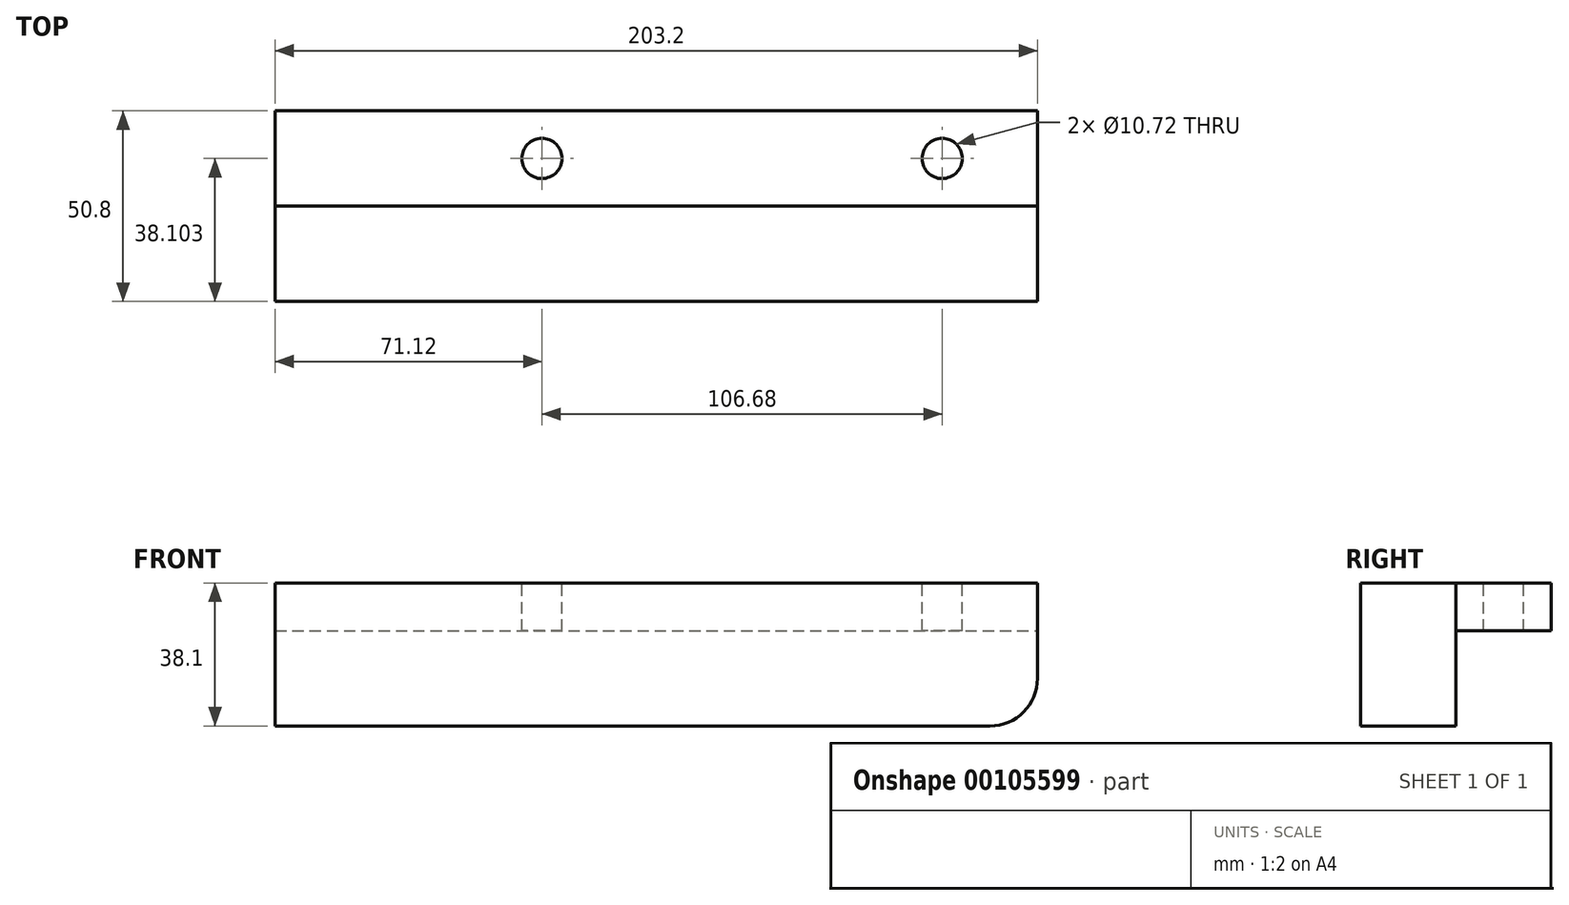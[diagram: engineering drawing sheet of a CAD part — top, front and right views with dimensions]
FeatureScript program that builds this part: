
annotation { "Feature Type Name" : "Feature", "Feature Type Description" : "" }
export const myFeature = defineFeature(function(context is Context, id is Id, definition is map)
    precondition{}
    {
        {
            var Q0;
            Q0=qCreatedBy(makeId("Top.planeOp"),FACE);
            var sketch = newSketch(context, id + "F0", { "sketchPlane" : qUnion([Q0])});
            skLineSegment(sketch, "E0.bottom", {"start": v(-101.6, 22.18) * mm, "end": v(101.6, 22.18) * mm});
            skLineSegment(sketch, "E0.top", {"start": v(-101.6, -28.62) * mm, "end": v(88.9, -28.62) * mm});
            skLineSegment(sketch, "E0.left", {"start": v(-101.6, 22.18) * mm, "end": v(-101.6, -28.62) * mm});
            skLineSegment(sketch, "E0.right", {"start": v(101.6, 22.18) * mm, "end": v(101.6, -15.92) * mm});
            skPoint(sketch, "E0.middle", {"position": v(0, -3.22) * mm});
            skLineSegment(sketch, "E1", {"start": v(-101.6, -3.22) * mm, "end": v(101.6, -3.22) * mm});
            skPoint(sketch, "E2.visualSharp", {"position": v(101.6, -28.62) * mm});
            skLineSegment(sketch, "E3", {"start": v(88.9, -28.62) * mm, "end": v(101.6, -28.62) * mm});
            skLineSegment(sketch, "E4", {"start": v(101.6, -15.92) * mm, "end": v(101.6, -28.62) * mm});
            skSolve(sketch);
        }
        {
            var Q0;
            {var subQ0=sQuery(id+"F0.wireOp",EDGE,"E0.bottom");Q0=makeQuery(id+"F0.imprint","IMPRINT",FACE,{"disambiguationData":[TD([[makeQuery(id+"F0.imprint","IMPRINT",EDGE,{"derivedFrom":subQ0}),-1.0]])]});}
            extrude(context, id + "F1", {"entities" : qUnion([Q0]), "oppositeDirection" : true, "depth" : 12.7 * mm});
        }
        {
            var Q0;
            {var subQ0=sQuery(id+"F0.wireOp",EDGE,"E0.top");Q0=makeQuery(id+"F0.imprint","IMPRINT",FACE,{"disambiguationData":[TD([[makeQuery(id+"F0.imprint","IMPRINT",EDGE,{"derivedFrom":subQ0}),1.0]])]});}
            extrude(context, id + "F2", {"entities" : qUnion([Q0]), "oppositeDirection" : true, "depth" : 38.1 * mm});
        }
        {
            var Q0;
            Q0=makeQuery(id+"F1.opExtrude","CAP_FACE",FACE,{"disambiguationData":[OSD([sQuery(id+"F0.wireOp",EDGE,"E0.bottom"),sQuery(id+"F0.wireOp",EDGE,"E0.left"),sQuery(id+"F0.wireOp",EDGE,"E0.right"),sQuery(id+"F0.wireOp",EDGE,"E1")])],"isStart":true});
            var sketch = newSketch(context, id + "F3", { "sketchPlane" : qUnion([Q0])});
            skPoint(sketch, "E5", {"position": v(76.2, 9.48) * mm});
            skPoint(sketch, "E6", {"position": v(-30.48, 9.48) * mm});
            skSolve(sketch);
        }
        {
            var Q0;
            Q0=sQuery(id+"F3.wireOp",VERTEX,"E6");
            var Q1;
            Q1=sQuery(id+"F3.wireOp",VERTEX,"E5");
            var Q2;
            Q2=makeQuery(id+"F1.opExtrude","SWEPT_BODY",BODY,{"disambiguationData":[OSD([sQuery(id+"F0.wireOp",EDGE,"E0.bottom"),sQuery(id+"F0.wireOp",EDGE,"E0.left"),sQuery(id+"F0.wireOp",EDGE,"E0.right"),sQuery(id+"F0.wireOp",EDGE,"E1")])]});
            hole(context, id + "F4", {"style" : HoleStyle.SIMPLE, "endStyle" : HoleEndStyle.BLIND, "holeDiameter" : 10.72 * mm, "holeDepth" : 50.8 * mm, "startFromSketch" : true, "locations" : qUnion([Q0, Q1]), "scope" : qUnion([Q2])});
        }
        {
            var Q0;
            Q0=makeQuery(id+"F2.opExtrude","CAP_EDGE",EDGE,{"disambiguationData":[OSD([sQuery(id+"F0.wireOp",EDGE,"E0.right"),sQuery(id+"F0.wireOp",EDGE,"E4")])],"isStart":false});
            fillet(context, id + "F5", {"entities" : qUnion([Q0]), "radius" : 12.7 * mm, "tangentPropagation" : true, "allowEdgeOverflow" : false});
        }
    });
